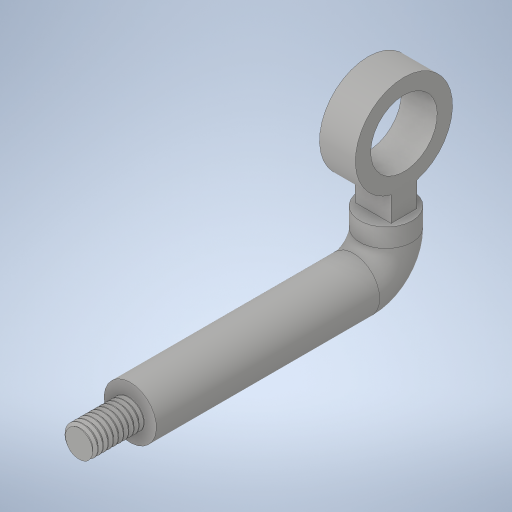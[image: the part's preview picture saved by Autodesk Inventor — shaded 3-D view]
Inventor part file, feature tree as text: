
AUTODESK INVENTOR PART (.ipt)
format: ipt  version: 2023 (Build 270158000, 158)  size: 411,136 bytes
history: mixed  units: in
note: dims shown in document units (in); Inventor stores cm internally (conversion verified against a paired STEP export)
features: sketch x3, plane x2, sweep x1, extrude x1, imported_body x1
ambient origin geometry x8: Origin, YZ Plane, XZ Plane, XY Plane, X Axis, Y Axis, Z Axis, Center Point
bodies: Solid6 (imported_parasolid), Body6 (imported_parasolid)
feature tree (8):
  sketch  "3D 草圖1"
  plane  "工作平面1"
  sweep  "掃掠1"
  plane  "工作平面2"
  extrude  "擠出2"  Depth=0.3937in
  sketch  "草圖4"
  sketch  "草圖7"
  imported_body  NMx_Import_Brep_tag  [imported B-rep: ~14 faces, bbox_mm=[8.61, 20.491381, 5.0]]
